# Revit family: Door_Sectional_Overhead_Glass
name_source: partatom
category: Doors
units: mm (PartAtom-declared; Revit-internal decimal feet)

## family parameters
Always vertical = Yes
Classification Number = 23.30.10.17.37.14
Cut with Voids When Loaded = No
Host = Wall
Room Calculation Point = No
Shared = No

## types (1)
- ByType
    Assembly Code = C1020100
    Building Codes = http://www.iccsafe.org
    CasingMaterial = ARCAT - Wood - Pine_Northern White
    CladdingMaterial = ARCAT - Metal - Aluminum_0.032" - Burgundy
    Construction Details = http://www.arcat.com
    Description = Sectional Overhead Door
    Door Thickness = 0' - 1 1/2"
    ENERGYSTAR Rating = North/Central
    Expected Lifespan (Years) = 15
    Fax = (203) 929-2444
    Fire Rating = 1 hour
    Frame Material = ARCAT - Metal - Steel 18ga - Painted - White
    Function = Interior
    Glass Thickness = 0' - 0 3/8"
    Glazing Type = ARCAT - Glass - Laminated - Tinted_Green
    Green Building-LEED = http://www.arcat.com
    HandleHeight = 3' - 0"
    Height = 9' - 0"
    JambMaterial = ARCAT - Wood - Douglas Fir
    JambThickness = 0' - 1 1/2"
    Keynote = 08360
    Maintenance Schedule (Months) = 36
    Manufacturer = Generic
    Model = Generic
    Panel Height = 1' - 1 1/2"
    Product Data = http://www.arcat.com
    Product Properties = http://www.arcat.com
    R_Value = 0
    Rough Height = 9' - 0"
    Rough Width = 8' - 0"
    SHGC = 0.54
    Sectional Panels = 8
    Specification = http://www.arcat.com
    Test Data = http://www.aamanet.org
    Thickness = 0' - 1 1/2"
    Track Length = 11' - 0"
    Track Material = ARCAT - Metal - Steel_Galvanized - 18ga
    Trackrad = 1' - 0"
    URL = http://www.arcat.com
    U_Factor = 0.39
    Usage = Exterior Closure
    Wall Closure = By host
    Warranty Duration (Years) = 10
    Width = 8' - 0"

## geometry (parser evidence)
native form markers: Blend x3, Sweep x6
no freeform markers — native parametric forms only
